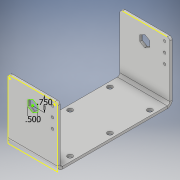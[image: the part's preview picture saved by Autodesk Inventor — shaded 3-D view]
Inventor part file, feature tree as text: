
AUTODESK INVENTOR PART (.ipt)
format: ipt  version: 2017 (Build 210142000, 142)  size: 221,184 bytes
history: native  units: in
note: dims shown in document units (in); Inventor stores cm internally (conversion verified against a paired STEP export)
features: sketch x9, other x8, sheet_metal_op x7, chamfer x1
ambient origin geometry x8: Origin, YZ Plane, XZ Plane, XY Plane, X Axis, Y Axis, Z Axis, Center Point
bodies: Solid1 (feature_tree)
feature tree (25):
  sheet_metal_op  "Face1"
  sheet_metal_op  "Flange1"
  sketch  "Sketch4"  dims[d3=0.125in]
  sketch  "Sketch5"  dims[d4=0.0625in]
  sheet_metal_op  "Flange2"
  chamfer  "Corner Round1"
  sketch  "Sketch1"  dims[d0=2.5in]
  other  "Plate1"
  sketch  "Sketch2"  dims[d1=3.0in]
  other  "Plate2"
  sheet_metal_op  "Bend1"
  sheet_metal_op  "Corner1"
  sketch  "Sketch3"  dims[d2=0.125in]
  sketch  "Sketch6"  dims[d5=0.25in]
  other  "Plate3"
  sheet_metal_op  "Bend2"
  sheet_metal_op  "Corner2"
  sketch  "Sketch7"  dims[d6=0.125in]
  sketch  "Sketch8"  dims[d7=5.75in d8=90.0deg d9=0.125in]
  sketch  "Sketch9"  dims[d10=0.5in d11=0.125in d12=0.125in d13=0.25in d15=0.25in d16=0.125in d17=0.0in d18=0.125in d24=0.125in d25=0.0625in d26=0.25in d27=0.125in d28=3.0in d29=90.0deg d30=0.125in d31=0.5in d32=0.125in d33=0.125in d36=0.125in d37=1.1811in d39=2.0in d40=0.7874in d42=2.0in d46=0.875in d51=0.5in d52=0.75in d53=0.125in d54=0.0in d55=0.125in d56=0.0in d57=0.125in d58=0.125in d59=0.125in d61=0.25in d62=0.5in d63=0.5in d64=0.125in d65=0.0in d66=0.125in d67=0.0in d68=0.255in]
  other  "Cut1"
  other  "Cut5"
  other  "Cut6"
  other  "Cut7"
  other  "Cut8"
